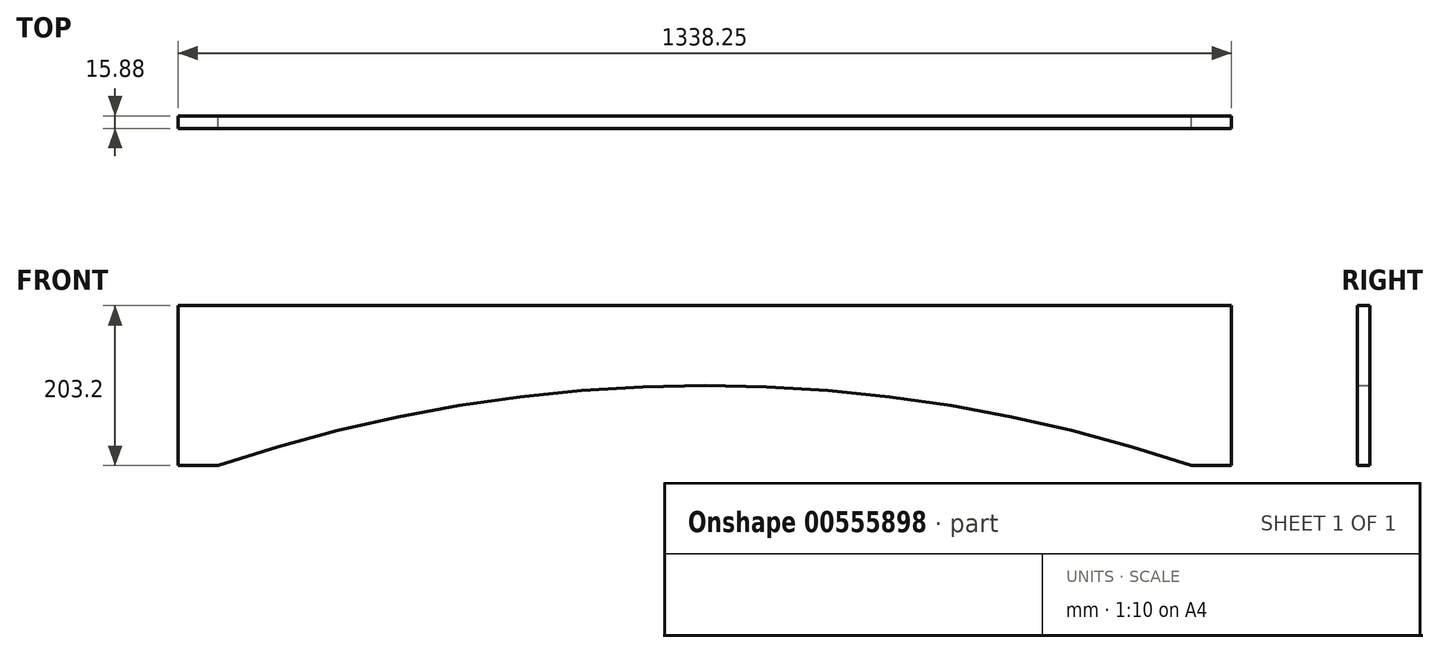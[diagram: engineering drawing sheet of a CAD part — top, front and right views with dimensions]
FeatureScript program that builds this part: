
annotation { "Feature Type Name" : "Feature", "Feature Type Description" : "" }
export const myFeature = defineFeature(function(context is Context, id is Id, definition is map)
    precondition{}
    {
        {
            var Q0;
            Q0=qCreatedBy(makeId("Front.planeOp"),FACE);
            var sketch = newSketch(context, id + "F0", { "sketchPlane" : qUnion([Q0])});
            skLineSegment(sketch, "E0", {"start": v(-50.8, 150.42) * mm, "end": v(1287.45, 150.42) * mm});
            skLineSegment(sketch, "E1", {"start": v(1287.45, 150.42) * mm, "end": v(1287.45, -52.78) * mm});
            skLineSegment(sketch, "E2", {"start": v(1287.45, -52.78) * mm, "end": v(1236.65, -52.78) * mm});
            skLineSegment(sketch, "E3", {"start": v(-50.8, 150.42) * mm, "end": v(-50.8, -52.78) * mm});
            skLineSegment(sketch, "E4", {"start": v(-50.8, -52.78) * mm, "end": v(0, -52.78) * mm});
            skArc(sketch, "E5", {"start": v(1236.65, -52.78) * mm, "mid": v(618.32, 48.82) * mm, "end": v(0, -52.78) * mm});
            skPoint(sketch, "E6.end.orphan", {"position": v(-50.8, 304.75) * mm});
            skPoint(sketch, "E7.start.orphan", {"position": v(618.32, 304.75) * mm});
            skPoint(sketch, "E8.start.orphan", {"position": v(618.32, 150.42) * mm});
            skSolve(sketch);
        }
        {
            var Q0;
            Q0 = qSketchRegion(id + "F0", true);
            extrude(context, id + "F1", {"entities" : qUnion([Q0]), "depth" : 15.88 * mm, "offsetDistance" : 25.4 * mm});
        }
    });
